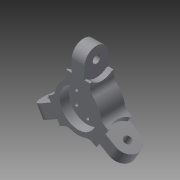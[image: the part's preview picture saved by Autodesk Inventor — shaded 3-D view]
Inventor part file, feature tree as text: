
AUTODESK INVENTOR PART (.ipt)
format: ipt  version: 2014 SP2 (Build 180246200, 246)  size: 241,152 bytes
history: native  units: mm
features: extrude x5, sketch x5, fillet x2, pattern_circular x2, mirror x1
ambient origin geometry x8: Origin, YZ Plane, XZ Plane, XY Plane, X Axis, Y Axis, Z Axis, Center Point
bodies: Solid1 (feature_tree)
feature tree (15):
  extrude  "Extrusion1"  TaperAngle=120.0deg  [1 undecoded]
  extrude  "Extrusion2"  Depth=26.0mm
  fillet  "Fillet1"  Radius=5.0mm
  extrude  "Extrusion3"  Depth=26.0mm
  mirror  "Mirror1"
  fillet  "Fillet2"  Radius=26.0mm
  pattern_circular  "Circular Pattern2"  [2 undecoded]
  extrude  "Extrusion4"  Depth=13.0mm
  pattern_circular  "Circular Pattern3"  [2 undecoded]
  extrude  "Extrusion6"  Depth=10.0mm
  sketch  "Sketch1"  dims[d0=50.0mm d1=120.0deg]
  sketch  "Sketch2"  dims[d2=120.0deg d3=26.0mm d4=5.0mm]
  sketch  "Sketch3"  dims[d5=30.0mm d6=14.0mm d7=26.0mm d8=0.0mm]
  sketch  "Sketch4"  dims[d12=8.0mm]
  sketch  "Sketch6"  dims[d13=13.0mm d14=15.0mm d15=0.0mm d16=13.0mm d17=15.0mm d18=0.0mm d19=10.0mm d20=30.0mm d21=360.0deg d23=28.0mm d24=4.0mm d25=15.0mm d26=0.0mm d30=60.0mm d31=360.0deg d33=40.0mm d34=10.0mm d35=0.0mm]
note: 5 required parameter values undecoded (feature->parameter linkage not recoverable at this tier; creation-order binding heuristic only, values carry confidence <= 0.55)
